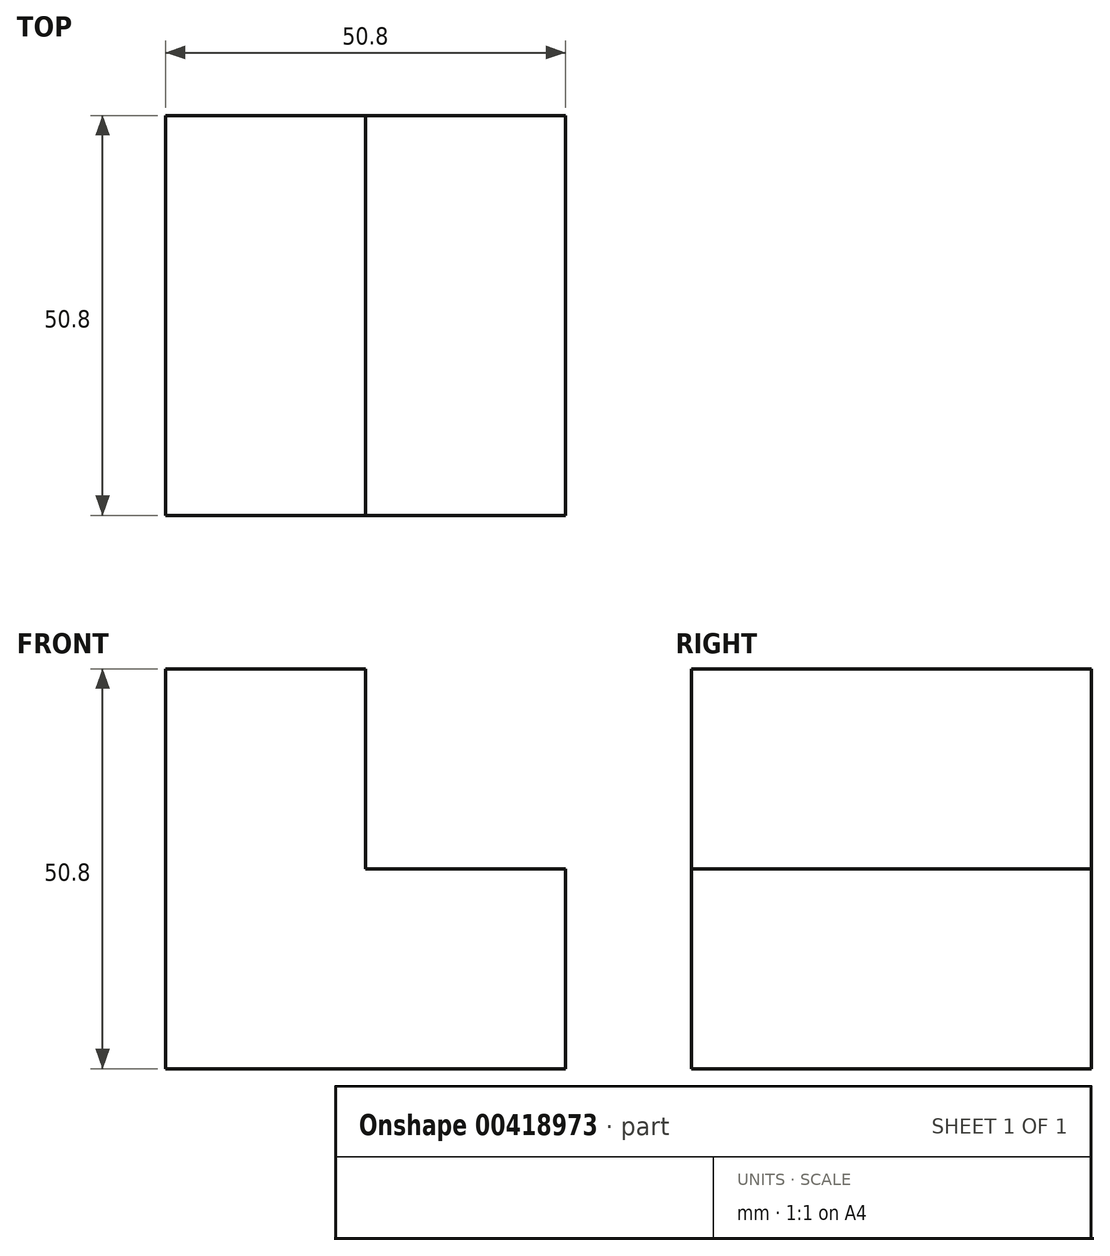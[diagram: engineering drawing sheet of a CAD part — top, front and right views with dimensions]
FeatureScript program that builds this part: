
annotation { "Feature Type Name" : "Feature", "Feature Type Description" : "" }
export const myFeature = defineFeature(function(context is Context, id is Id, definition is map)
    precondition{}
    {
        {
            var Q0;
            Q0=qCreatedBy(makeId("Front.planeOp"),FACE);
            var sketch = newSketch(context, id + "F0", { "sketchPlane" : qUnion([Q0])});
            skLineSegment(sketch, "E0", {"start": v(0, 0) * mm, "end": v(-50.8, 0) * mm});
            skLineSegment(sketch, "E1", {"start": v(-50.8, 0) * mm, "end": v(-50.8, 50.8) * mm});
            skLineSegment(sketch, "E2", {"start": v(-50.8, 50.8) * mm, "end": v(-25.4, 50.8) * mm});
            skLineSegment(sketch, "E3", {"start": v(-25.4, 50.8) * mm, "end": v(-25.4, 25.4) * mm});
            skLineSegment(sketch, "E4", {"start": v(-25.4, 25.4) * mm, "end": v(0, 25.4) * mm});
            skLineSegment(sketch, "E5", {"start": v(0, 25.4) * mm, "end": v(0, 0) * mm});
            skLineSegment(sketch, "E6", {"start": v(-25.4, 25.4) * mm, "end": v(-25.4, -25.4) * mm});
            skLineSegment(sketch, "E7", {"start": v(0, 25.4) * mm, "end": v(0, -25.4) * mm});
            skSolve(sketch);
        }
        {
            var Q0;
            Q0 = qSketchRegion(id + "F0", true);
            extrude(context, id + "F1", {"entities" : qUnion([Q0]), "depth" : 50.8 * mm});
        }
    });
